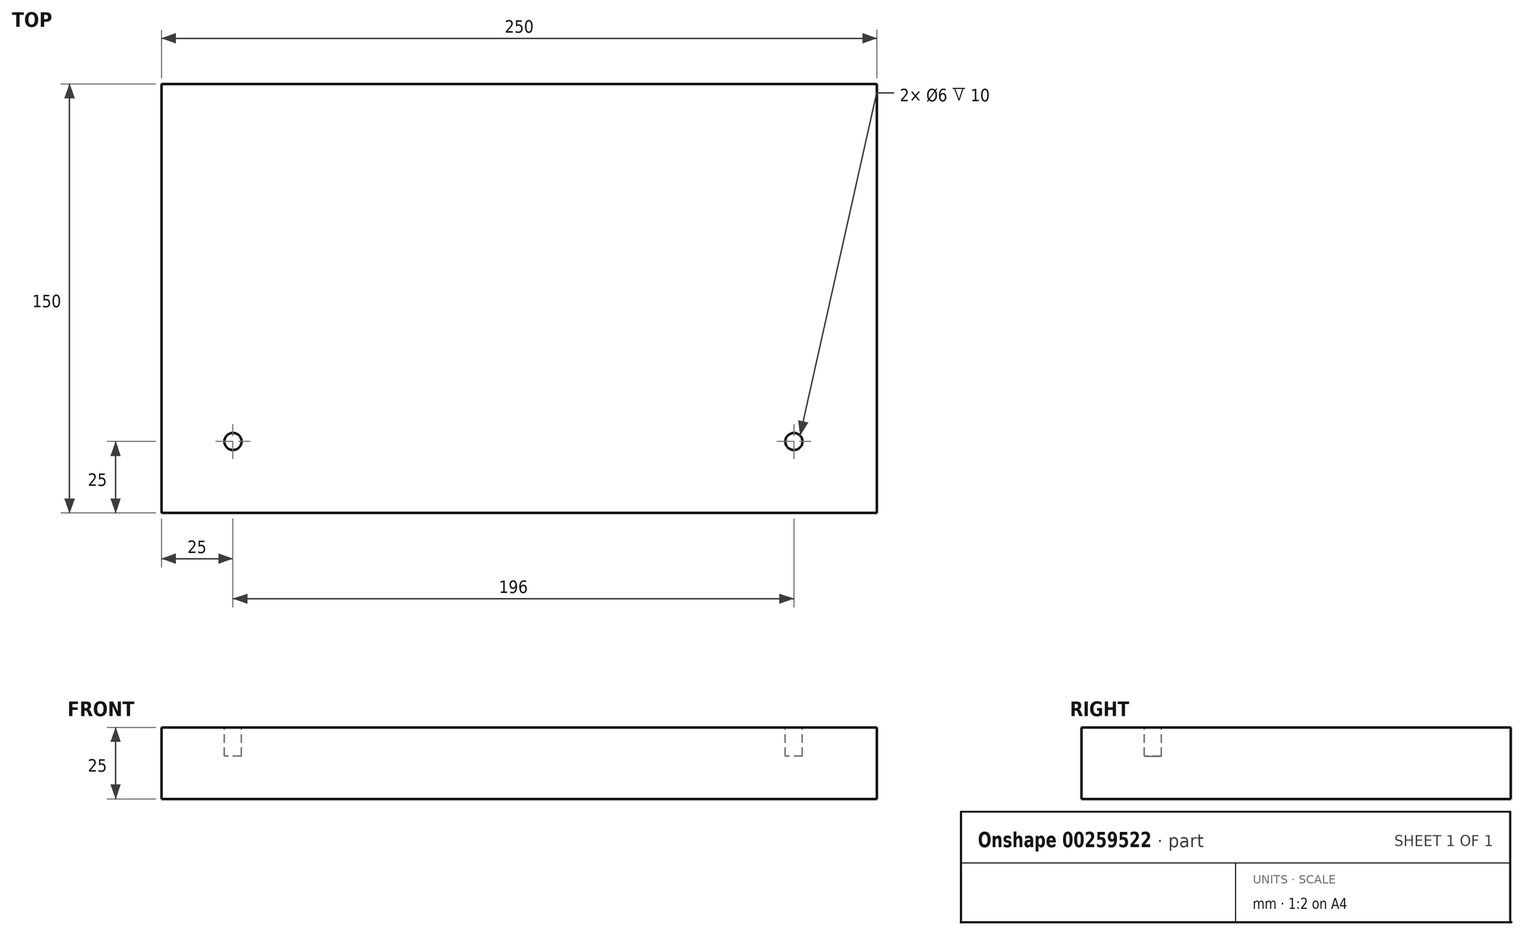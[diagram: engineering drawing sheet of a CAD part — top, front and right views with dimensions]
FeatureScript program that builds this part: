
annotation { "Feature Type Name" : "Feature", "Feature Type Description" : "" }
export const myFeature = defineFeature(function(context is Context, id is Id, definition is map)
    precondition{}
    {
        {
            var Q0;
            Q0=qCreatedBy(makeId("Top.planeOp"),FACE);
            var sketch = newSketch(context, id + "F0", { "sketchPlane" : qUnion([Q0])});
            skLineSegment(sketch, "E0.bottom", {"start": v(0, 0) * mm, "end": v(250, 0) * mm});
            skLineSegment(sketch, "E0.top", {"start": v(0, 150) * mm, "end": v(250, 150) * mm});
            skLineSegment(sketch, "E0.left", {"start": v(0, 0) * mm, "end": v(0, 150) * mm});
            skLineSegment(sketch, "E0.right", {"start": v(250, 0) * mm, "end": v(250, 150) * mm});
            skSolve(sketch);
        }
        {
            var Q0;
            Q0=makeQuery(id+"F0.imprint","IMPRINT",FACE,{"disambiguationData":[TD([[makeQuery(id+"F0.imprint","IMPRINT",EDGE,{"derivedFrom":sQuery(id+"F0.wireOp",EDGE,"E0.bottom")}),1.0]])]});
            extrude(context, id + "F1", {"entities" : qUnion([Q0]), "depth" : 25 * mm});
        }
        {
            var Q0;
            Q0=makeQuery(id+"F1.opExtrude","CAP_FACE",FACE,{"disambiguationData":[OSD([sQuery(id+"F0.wireOp",EDGE,"E0.bottom"),sQuery(id+"F0.wireOp",EDGE,"E0.top"),sQuery(id+"F0.wireOp",EDGE,"E0.left"),sQuery(id+"F0.wireOp",EDGE,"E0.right")])],"isStart":false});
            var sketch = newSketch(context, id + "F2", { "sketchPlane" : qUnion([Q0])});
            skPoint(sketch, "E1", {"position": v(25, 25) * mm});
            skPoint(sketch, "E2", {"position": v(221, 25) * mm});
            skLineSegment(sketch, "E3", {"start": v(25, 25) * mm, "end": v(25, 126.67) * mm, "construction": true});
            skCircle(sketch, "E4", {"center": v(25, 25) * mm, "radius": 3 * mm});
            skCircle(sketch, "E5", {"center": v(221, 25) * mm, "radius": 3 * mm});
            skSolve(sketch);
        }
        {
            var Q0;
            Q0 = qSketchRegion(id + "F2", true);
            extrude(context, id + "F3", {"entities" : qUnion([Q0]), "operationType" : NewBodyOperationType.REMOVE, "oppositeDirection" : true, "depth" : 10 * mm});
        }
    });
